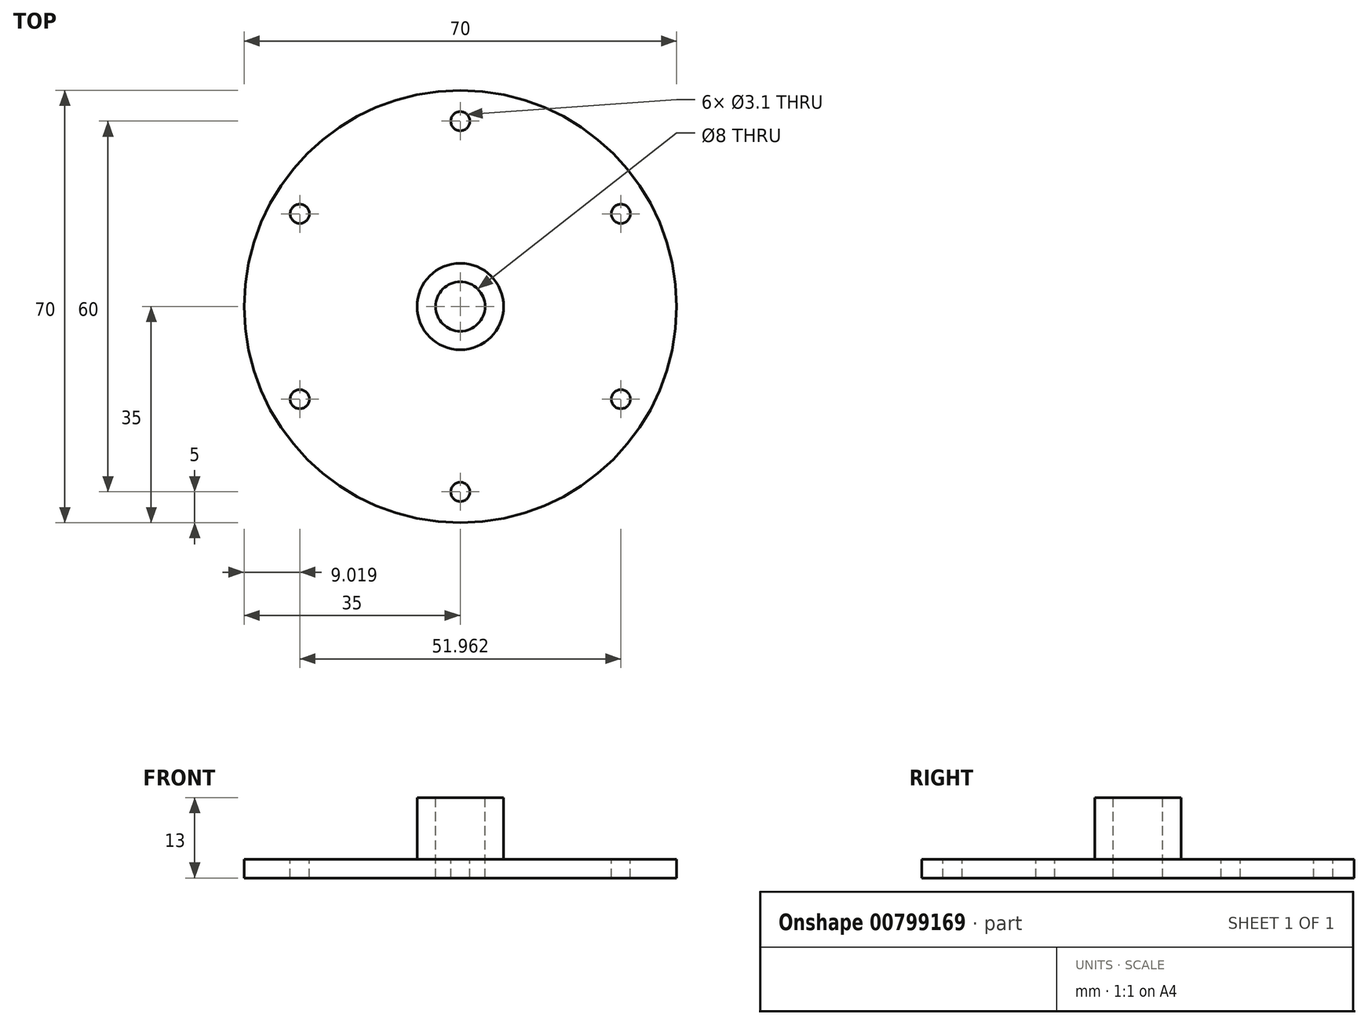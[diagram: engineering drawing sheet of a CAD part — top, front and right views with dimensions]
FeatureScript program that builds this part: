
annotation { "Feature Type Name" : "Feature", "Feature Type Description" : "" }
export const myFeature = defineFeature(function(context is Context, id is Id, definition is map)
    precondition{}
    {
        {
            var Q0;
            Q0=qCreatedBy(makeId("Top.planeOp"),FACE);
            var sketch = newSketch(context, id + "F0", { "sketchPlane" : qUnion([Q0])});
            skCircle(sketch, "E0", {"center": v(0, 0) * mm, "radius": 35 * mm});
            skSolve(sketch);
        }
        {
            var Q0;
            Q0=makeQuery(id+"F0.imprint","IMPRINT",FACE,{"disambiguationData":[TD([[makeQuery(id+"F0.imprint","IMPRINT",EDGE,{"derivedFrom":sQuery(id+"F0.wireOp",EDGE,"E0")}),1.0]])]});
            extrude(context, id + "F1", {"entities" : qUnion([Q0]), "depth" : 3 * mm, "offsetDistance" : 25 * mm});
        }
        {
            var Q0;
            Q0=makeQuery(id+"F1.opExtrude","CAP_FACE",FACE,{"disambiguationData":[OSD([sQuery(id+"F0.wireOp",EDGE,"E0")])],"isStart":false});
            var sketch = newSketch(context, id + "F2", { "sketchPlane" : qUnion([Q0])});
            skCircle(sketch, "E1", {"center": v(0, 30) * mm, "radius": 1.55 * mm});
            skCircle(sketch, "E2.1.0", {"center": v(-25.98, 15) * mm, "radius": 1.55 * mm});
            skCircle(sketch, "E2.2.0", {"center": v(-25.98, -15) * mm, "radius": 1.55 * mm});
            skPoint(sketch, "E2.center", {"position": v(0, 0) * mm});
            skCircle(sketch, "E3.1.3.0", {"center": v(0, -30) * mm, "radius": 1.55 * mm});
            skCircle(sketch, "E3.1.4.0", {"center": v(25.98, -15) * mm, "radius": 1.55 * mm});
            skCircle(sketch, "E3.1.5.0", {"center": v(25.98, 15) * mm, "radius": 1.55 * mm});
            skSolve(sketch);
        }
        {
            var Q0;
            Q0=makeQuery(id+"F2.imprint","IMPRINT",FACE,{"disambiguationData":[TD([[makeQuery(id+"F2.imprint","IMPRINT",EDGE,{"derivedFrom":sQuery(id+"F2.wireOp",EDGE,"E1")}),1.0]])]});
            var Q1;
            Q1=makeQuery(id+"F2.imprint","IMPRINT",FACE,{"disambiguationData":[TD([[makeQuery(id+"F2.imprint","IMPRINT",EDGE,{"derivedFrom":sQuery(id+"F2.wireOp",EDGE,"E2.1.0")}),1.0]])]});
            var Q2;
            Q2=makeQuery(id+"F2.imprint","IMPRINT",FACE,{"disambiguationData":[TD([[makeQuery(id+"F2.imprint","IMPRINT",EDGE,{"derivedFrom":sQuery(id+"F2.wireOp",EDGE,"E2.2.0")}),1.0]])]});
            var Q3;
            Q3=makeQuery(id+"F2.imprint","IMPRINT",FACE,{"disambiguationData":[TD([[makeQuery(id+"F2.imprint","IMPRINT",EDGE,{"derivedFrom":sQuery(id+"F2.wireOp",EDGE,"E3.1.5.0")}),1.0]])]});
            var Q4;
            Q4=makeQuery(id+"F2.imprint","IMPRINT",FACE,{"disambiguationData":[TD([[makeQuery(id+"F2.imprint","IMPRINT",EDGE,{"derivedFrom":sQuery(id+"F2.wireOp",EDGE,"E3.1.4.0")}),1.0]])]});
            var Q5;
            Q5=makeQuery(id+"F2.imprint","IMPRINT",FACE,{"disambiguationData":[TD([[makeQuery(id+"F2.imprint","IMPRINT",EDGE,{"derivedFrom":sQuery(id+"F2.wireOp",EDGE,"E3.1.3.0")}),1.0]])]});
            extrude(context, id + "F3", {"entities" : qUnion([Q0, Q1, Q2, Q3, Q4, Q5]), "operationType" : NewBodyOperationType.REMOVE, "endBound" : BoundingType.THROUGH_ALL, "oppositeDirection" : true, "depth" : 25 * mm, "offsetDistance" : 25 * mm});
        }
        {
            var Q0;
            Q0=makeQuery(id+"F1.opExtrude","CAP_FACE",FACE,{"disambiguationData":[OSD([sQuery(id+"F0.wireOp",EDGE,"E0")])],"isStart":false});
            var sketch = newSketch(context, id + "F4", { "sketchPlane" : qUnion([Q0])});
            skCircle(sketch, "E4", {"center": v(0, 0) * mm, "radius": 7 * mm});
            skSolve(sketch);
        }
        {
            var Q0;
            Q0=makeQuery(id+"F4.imprint","IMPRINT",FACE,{"disambiguationData":[TD([[makeQuery(id+"F4.imprint","IMPRINT",EDGE,{"derivedFrom":sQuery(id+"F4.wireOp",EDGE,"E4")}),1.0]])]});
            extrude(context, id + "F5", {"entities" : qUnion([Q0]), "operationType" : NewBodyOperationType.ADD, "depth" : 10 * mm, "offsetDistance" : 25 * mm});
        }
        {
            var Q0;
            Q0=makeQuery(id+"F5.opExtrude","CAP_FACE",FACE,{"disambiguationData":[OSD([sQuery(id+"F4.wireOp",EDGE,"E4")])],"isStart":false});
            var sketch = newSketch(context, id + "F6", { "sketchPlane" : qUnion([Q0])});
            skCircle(sketch, "E5", {"center": v(0, 0) * mm, "radius": 4 * mm});
            skSolve(sketch);
        }
        {
            var Q0;
            Q0=makeQuery(id+"F6.imprint","IMPRINT",FACE,{"disambiguationData":[TD([[makeQuery(id+"F6.imprint","IMPRINT",EDGE,{"derivedFrom":sQuery(id+"F6.wireOp",EDGE,"E5")}),1.0]])]});
            extrude(context, id + "F7", {"entities" : qUnion([Q0]), "operationType" : NewBodyOperationType.REMOVE, "endBound" : BoundingType.THROUGH_ALL, "oppositeDirection" : true, "depth" : 8 * mm, "offsetDistance" : 25 * mm});
        }
    });
